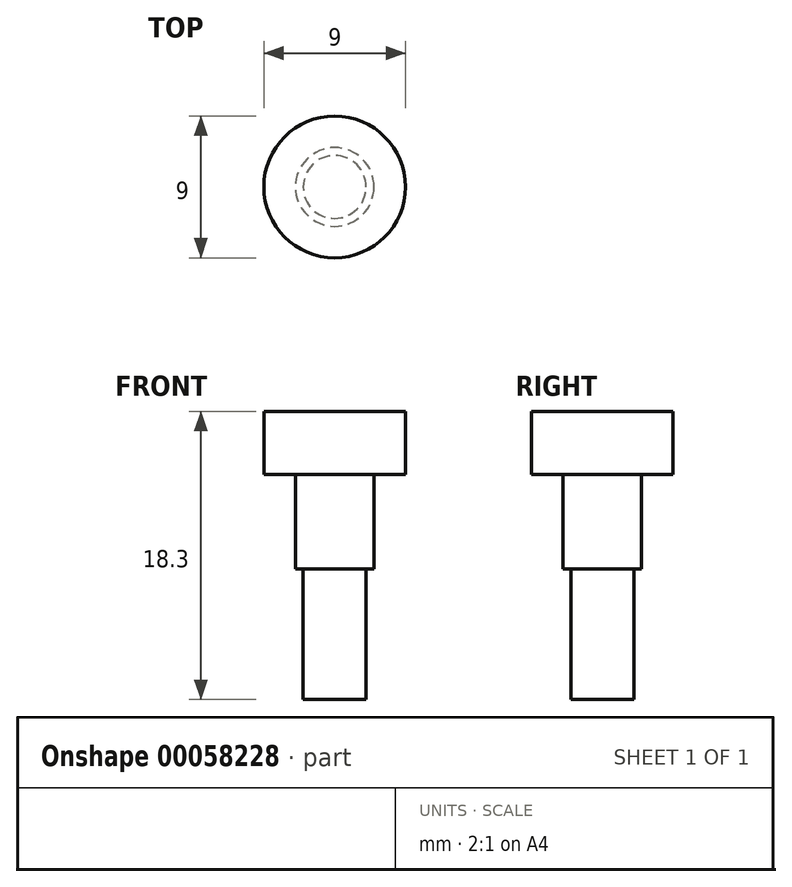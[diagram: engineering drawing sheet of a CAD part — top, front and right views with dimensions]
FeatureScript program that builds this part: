
annotation { "Feature Type Name" : "Feature", "Feature Type Description" : "" }
export const myFeature = defineFeature(function(context is Context, id is Id, definition is map)
    precondition{}
    {
        {
            var Q0;
            Q0=qCreatedBy(makeId("Front.planeOp"),FACE);
            var sketch = newSketch(context, id + "F0", { "sketchPlane" : qUnion([Q0])});
            skLineSegment(sketch, "E0", {"start": v(0, 0) * mm, "end": v(0, 18.3) * mm});
            skLineSegment(sketch, "E1", {"start": v(0, 18.3) * mm, "end": v(4.5, 18.3) * mm});
            skLineSegment(sketch, "E2", {"start": v(4.5, 18.3) * mm, "end": v(4.5, 14.3) * mm});
            skLineSegment(sketch, "E3", {"start": v(4.5, 14.3) * mm, "end": v(2.5, 14.3) * mm});
            skLineSegment(sketch, "E4", {"start": v(2.5, 14.3) * mm, "end": v(2.5, 8.3) * mm});
            skLineSegment(sketch, "E5", {"start": v(2.5, 8.3) * mm, "end": v(2, 8.3) * mm});
            skLineSegment(sketch, "E6", {"start": v(2, 8.3) * mm, "end": v(2, 0) * mm});
            skLineSegment(sketch, "E7", {"start": v(2, 0) * mm, "end": v(0, 0) * mm});
            skSolve(sketch);
        }
        {
            var Q0;
            Q0 = qSketchRegion(id + "F0", true);
            var Q1;
            Q1=sQuery(id+"F0.wireOp",EDGE,"E0");
            revolve(context, id + "F1", {"entities" : qUnion([Q0]), "axis" : qUnion([Q1]), "revolveType" : RevolveType.FULL});
        }
    });
